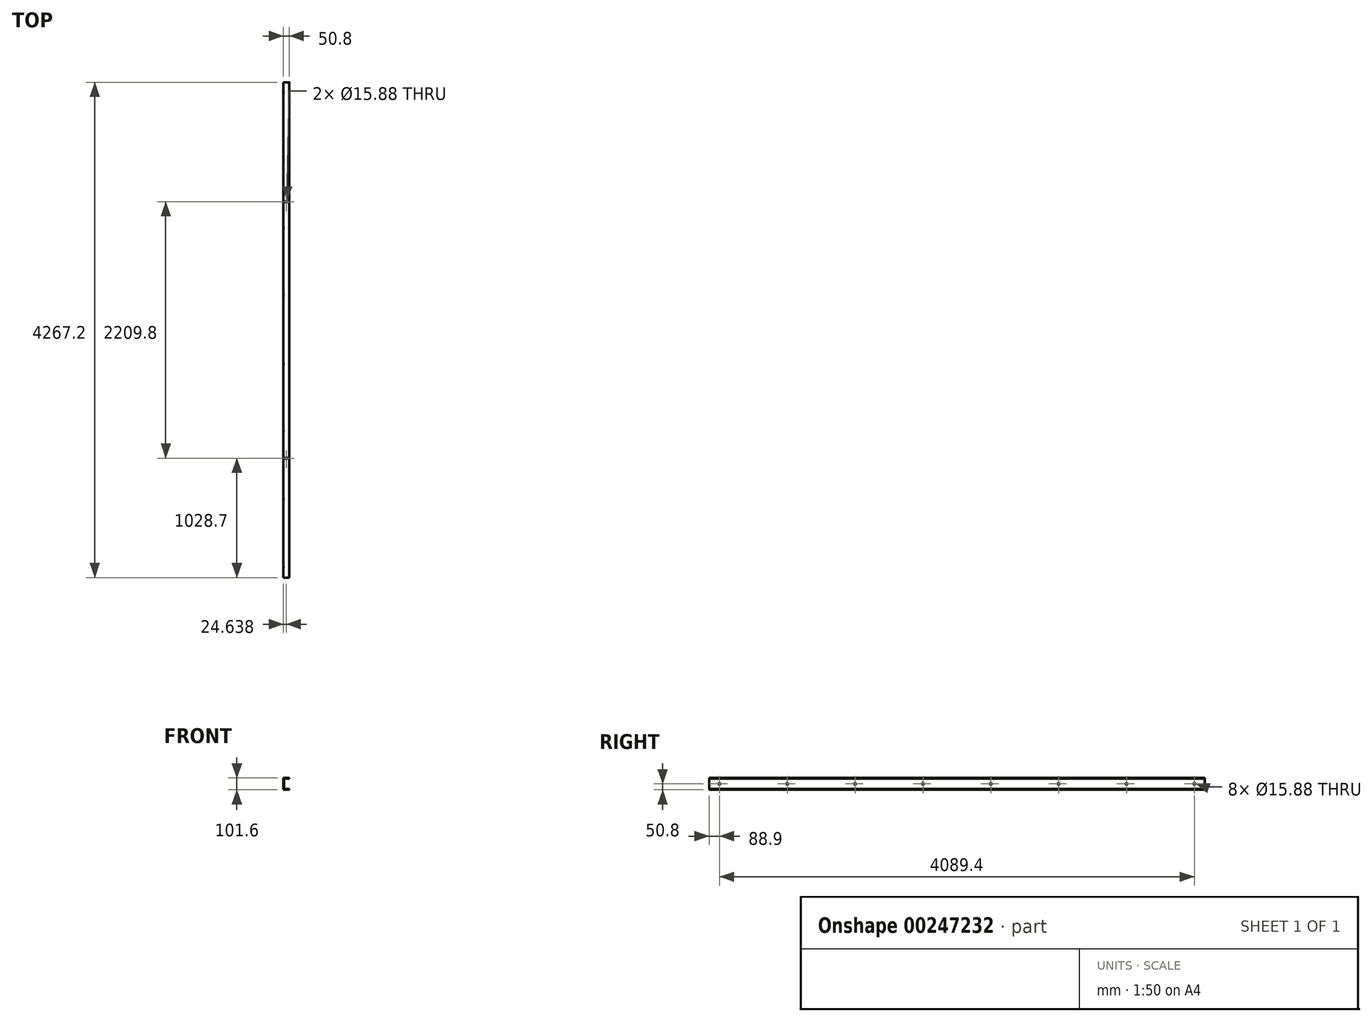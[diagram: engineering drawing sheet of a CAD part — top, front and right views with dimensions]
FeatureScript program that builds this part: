
annotation { "Feature Type Name" : "Feature", "Feature Type Description" : "" }
export const myFeature = defineFeature(function(context is Context, id is Id, definition is map)
    precondition{}
    {
        {
            var Q0;
            Q0=qCreatedBy(makeId("Front.planeOp"),FACE);
            var sketch = newSketch(context, id + "F0", { "sketchPlane" : qUnion([Q0])});
            skLineSegment(sketch, "E0", {"start": v(0, 0) * mm, "end": v(49.28, 0) * mm});
            skLineSegment(sketch, "E1", {"start": v(50.8, 1.52) * mm, "end": v(50.8, 4.83) * mm});
            skLineSegment(sketch, "E2", {"start": v(49.28, 6.35) * mm, "end": v(7.87, 6.35) * mm});
            skLineSegment(sketch, "E3", {"start": v(6.35, 7.87) * mm, "end": v(6.35, 93.73) * mm});
            skLineSegment(sketch, "E4", {"start": v(7.87, 95.25) * mm, "end": v(49.28, 95.25) * mm});
            skLineSegment(sketch, "E5", {"start": v(50.8, 96.77) * mm, "end": v(50.8, 100.08) * mm});
            skLineSegment(sketch, "E6", {"start": v(49.28, 101.6) * mm, "end": v(0, 101.6) * mm});
            skLineSegment(sketch, "E7", {"start": v(0, 101.6) * mm, "end": v(0, 0) * mm});
            skPoint(sketch, "E8.visualSharp", {"position": v(6.35, 95.25) * mm});
            skArc(sketch, "E8.filletArc", {"start": v(7.87, 95.25) * mm, "mid": v(6.8, 94.8) * mm, "end": v(6.35, 93.73) * mm});
            skPoint(sketch, "E9.visualSharp", {"position": v(50.8, 95.25) * mm});
            skArc(sketch, "E9.filletArc", {"start": v(49.28, 95.25) * mm, "mid": v(50.35, 95.7) * mm, "end": v(50.8, 96.77) * mm});
            skPoint(sketch, "E10.visualSharp", {"position": v(50.8, 101.6) * mm});
            skArc(sketch, "E10.filletArc", {"start": v(50.8, 100.08) * mm, "mid": v(50.35, 101.15) * mm, "end": v(49.28, 101.6) * mm});
            skPoint(sketch, "E11.visualSharp", {"position": v(50.8, 6.35) * mm});
            skArc(sketch, "E11.filletArc", {"start": v(50.8, 4.83) * mm, "mid": v(50.35, 5.9) * mm, "end": v(49.28, 6.35) * mm});
            skPoint(sketch, "E12.visualSharp", {"position": v(50.8, 0) * mm});
            skArc(sketch, "E12.filletArc", {"start": v(49.28, 0) * mm, "mid": v(50.35, 0.45) * mm, "end": v(50.8, 1.52) * mm});
            skPoint(sketch, "E13.visualSharp", {"position": v(6.35, 6.35) * mm});
            skArc(sketch, "E13.filletArc", {"start": v(6.35, 7.87) * mm, "mid": v(6.8, 6.8) * mm, "end": v(7.87, 6.35) * mm});
            skSolve(sketch);
        }
        {
            var Q0;
            Q0=makeQuery(id+"F0.imprint","IMPRINT",FACE,{"disambiguationData":[TD([[makeQuery(id+"F0.imprint","IMPRINT",EDGE,{"derivedFrom":sQuery(id+"F0.wireOp",EDGE,"E0")}),1.0]])]});
            extrude(context, id + "F1", {"entities" : qUnion([Q0]), "depth" : 4267.2 * mm});
        }
        {
            var Q0;
            Q0=makeQuery(id+"F1.opExtrude","SWEPT_FACE",FACE,{"disambiguationData":[OSD([sQuery(id+"F0.wireOp",EDGE,"E6")])]});
            var sketch = newSketch(context, id + "F2", { "sketchPlane" : qUnion([Q0])});
            skPoint(sketch, "E14", {"position": v(24.64, -3238.5) * mm});
            skPoint(sketch, "E14.positionSnap0", {"position": v(24.64, -4267.2) * mm});
            skPoint(sketch, "E15", {"position": v(24.64, -1028.7) * mm});
            skPoint(sketch, "E15.positionSnap0", {"position": v(24.64, 0) * mm});
            skSolve(sketch);
        }
        {
            var Q0;
            Q0=sQuery(id+"F2.wireOp",VERTEX,"E14");
            var Q1;
            Q1=sQuery(id+"F2.wireOp",VERTEX,"E15");
            var Q2;
            Q2=makeQuery(id+"F1.opExtrude","SWEPT_BODY",BODY,{"disambiguationData":[OSD([sQuery(id+"F0.wireOp",EDGE,"E0"),sQuery(id+"F0.wireOp",EDGE,"E1"),sQuery(id+"F0.wireOp",EDGE,"E2"),sQuery(id+"F0.wireOp",EDGE,"E3"),sQuery(id+"F0.wireOp",EDGE,"E4"),sQuery(id+"F0.wireOp",EDGE,"E5"),sQuery(id+"F0.wireOp",EDGE,"E6"),sQuery(id+"F0.wireOp",EDGE,"E7"),sQuery(id+"F0.wireOp",EDGE,"E9.filletArc"),sQuery(id+"F0.wireOp",EDGE,"E10.filletArc"),sQuery(id+"F0.wireOp",EDGE,"E11.filletArc"),sQuery(id+"F0.wireOp",EDGE,"E12.filletArc"),sQuery(id+"F0.wireOp",EDGE,"E13.filletArc"),sQuery(id+"F0.wireOp",EDGE,"E8.filletArc")])]});
            hole(context, id + "F3", {"style" : HoleStyle.SIMPLE, "endStyle" : HoleEndStyle.BLIND, "holeDiameter" : 15.88 * mm, "holeDepth" : 6.35 * mm, "tappedDepth" : 12.7 * mm, "tapClearance" : 3, "locations" : qUnion([Q0, Q1]), "scope" : qUnion([Q2])});
        }
        {
            var Q0;
            Q0=makeQuery(id+"F1.opExtrude","SWEPT_FACE",FACE,{"disambiguationData":[OSD([sQuery(id+"F0.wireOp",EDGE,"E7")])]});
            var sketch = newSketch(context, id + "F4", { "sketchPlane" : qUnion([Q0])});
            skPoint(sketch, "E16", {"position": v(88.9, 50.8) * mm});
            skPoint(sketch, "E16.positionSnap0", {"position": v(0, 50.8) * mm});
            skPoint(sketch, "E17.1.0.0", {"position": v(673.1, 50.8) * mm});
            skPoint(sketch, "E17.2.0.0", {"position": v(1257.3, 50.8) * mm});
            skPoint(sketch, "E17.3.0.0", {"position": v(1841.5, 50.8) * mm});
            skPoint(sketch, "E17.4.0.0", {"position": v(2425.7, 50.8) * mm});
            skPoint(sketch, "E17.5.0.0", {"position": v(3009.9, 50.8) * mm});
            skPoint(sketch, "E17.6.0.0", {"position": v(3594.1, 50.8) * mm});
            skPoint(sketch, "E17.7.0.0", {"position": v(4178.3, 50.8) * mm});
            skLineSegment(sketch, "E17.direction1", {"start": v(88.9, 50.8) * mm, "end": v(673.1, 50.8) * mm, "construction": true});
            skSolve(sketch);
        }
        {
            var Q0;
            Q0=sQuery(id+"F4.wireOp",VERTEX,"E16");
            var Q1;
            Q1=sQuery(id+"F4.wireOp",VERTEX,"E17.1.0.0");
            var Q2;
            Q2=sQuery(id+"F4.wireOp",VERTEX,"E17.2.0.0");
            var Q3;
            Q3=sQuery(id+"F4.wireOp",VERTEX,"E17.3.0.0");
            var Q4;
            Q4=sQuery(id+"F4.wireOp",VERTEX,"E17.4.0.0");
            var Q5;
            Q5=sQuery(id+"F4.wireOp",VERTEX,"E17.5.0.0");
            var Q6;
            Q6=sQuery(id+"F4.wireOp",VERTEX,"E17.6.0.0");
            var Q7;
            Q7=sQuery(id+"F4.wireOp",VERTEX,"E17.7.0.0");
            var Q8;
            Q8=makeQuery(id+"F1.opExtrude","SWEPT_BODY",BODY,{"disambiguationData":[OSD([sQuery(id+"F0.wireOp",EDGE,"E0"),sQuery(id+"F0.wireOp",EDGE,"E1"),sQuery(id+"F0.wireOp",EDGE,"E2"),sQuery(id+"F0.wireOp",EDGE,"E3"),sQuery(id+"F0.wireOp",EDGE,"E4"),sQuery(id+"F0.wireOp",EDGE,"E5"),sQuery(id+"F0.wireOp",EDGE,"E6"),sQuery(id+"F0.wireOp",EDGE,"E7"),sQuery(id+"F0.wireOp",EDGE,"E9.filletArc"),sQuery(id+"F0.wireOp",EDGE,"E10.filletArc"),sQuery(id+"F0.wireOp",EDGE,"E11.filletArc"),sQuery(id+"F0.wireOp",EDGE,"E12.filletArc"),sQuery(id+"F0.wireOp",EDGE,"E13.filletArc"),sQuery(id+"F0.wireOp",EDGE,"E8.filletArc")])]});
            hole(context, id + "F5", {"style" : HoleStyle.SIMPLE, "endStyle" : HoleEndStyle.BLIND, "holeDiameter" : 15.88 * mm, "holeDepth" : 6.35 * mm, "tappedDepth" : 12.7 * mm, "tapClearance" : 3, "locations" : qUnion([Q0, Q1, Q2, Q3, Q4, Q5, Q6, Q7]), "scope" : qUnion([Q8])});
        }
    });
